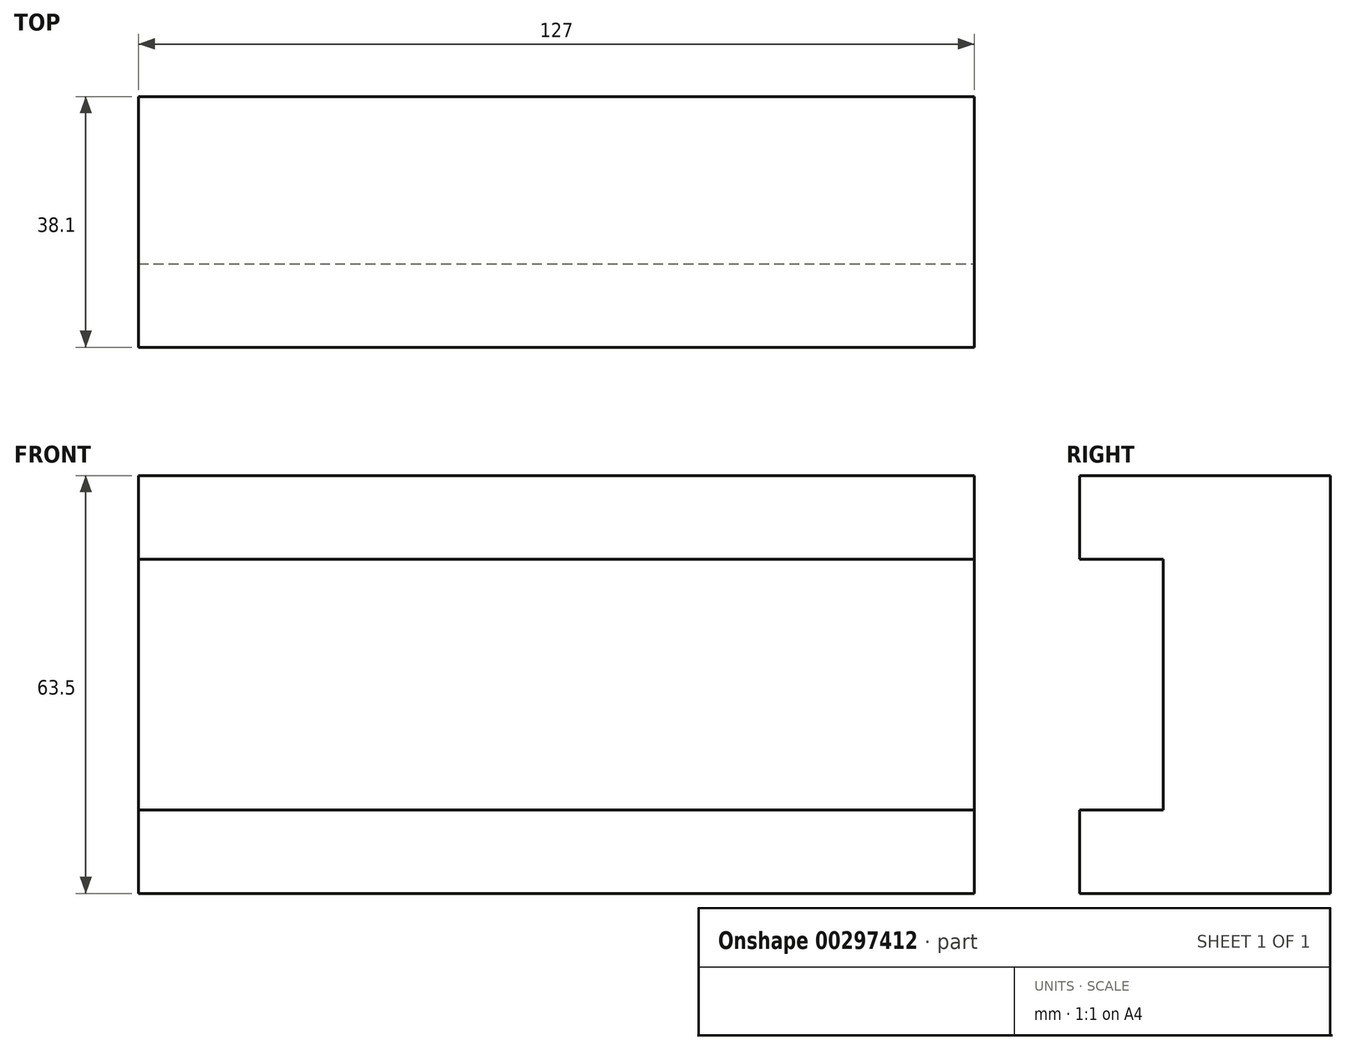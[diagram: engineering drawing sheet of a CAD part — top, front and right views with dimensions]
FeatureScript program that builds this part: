
annotation { "Feature Type Name" : "Feature", "Feature Type Description" : "" }
export const myFeature = defineFeature(function(context is Context, id is Id, definition is map)
    precondition{}
    {
        {
            var Q0;
            Q0=qCreatedBy(makeId("Front.planeOp"),FACE);
            var sketch = newSketch(context, id + "F0", { "sketchPlane" : qUnion([Q0])});
            skLineSegment(sketch, "E0.bottom", {"start": v(-63.5, -31.75) * mm, "end": v(63.5, -31.75) * mm});
            skLineSegment(sketch, "E0.top", {"start": v(-63.5, 31.75) * mm, "end": v(63.5, 31.75) * mm});
            skLineSegment(sketch, "E0.left", {"start": v(-63.5, -31.75) * mm, "end": v(-63.5, 31.75) * mm});
            skLineSegment(sketch, "E0.right", {"start": v(63.5, -31.75) * mm, "end": v(63.5, 31.75) * mm});
            skPoint(sketch, "E0.middle", {"position": v(0, 0) * mm});
            skLineSegment(sketch, "E1.top", {"start": v(-63.5, 19.05) * mm, "end": v(63.5, 19.05) * mm});
            skLineSegment(sketch, "E1.left", {"start": v(-63.5, 31.75) * mm, "end": v(-63.5, 19.05) * mm});
            skLineSegment(sketch, "E1.right", {"start": v(63.5, 31.75) * mm, "end": v(63.5, 19.05) * mm});
            skLineSegment(sketch, "E2.bottom", {"start": v(-63.5, -19.05) * mm, "end": v(63.5, -19.05) * mm});
            skLineSegment(sketch, "E2.left", {"start": v(-63.5, -19.05) * mm, "end": v(-63.5, -31.75) * mm});
            skLineSegment(sketch, "E2.right", {"start": v(63.5, -19.05) * mm, "end": v(63.5, -31.75) * mm});
            skSolve(sketch);
        }
        {
            var Q0;
            Q0 = qSketchRegion(id + "F0", true);
            extrude(context, id + "F1", {"entities" : qUnion([Q0]), "depth" : 25.4 * mm});
        }
        {
            var Q0;
            Q0=makeQuery(id+"F1.opExtrude","CAP_FACE",FACE,{"disambiguationData":[OSD([sQuery(id+"F0.wireOp",EDGE,"E0.left"),sQuery(id+"F0.wireOp",EDGE,"E0.right"),sQuery(id+"F0.wireOp",EDGE,"E0.top"),sQuery(id+"F0.wireOp",EDGE,"E1.left"),sQuery(id+"F0.wireOp",EDGE,"E1.right"),sQuery(id+"F0.wireOp",EDGE,"E0.bottom"),sQuery(id+"F0.wireOp",EDGE,"E2.left"),sQuery(id+"F0.wireOp",EDGE,"E2.right")])],"isStart":false});
            var sketch = newSketch(context, id + "F2", { "sketchPlane" : qUnion([Q0])});
            skLineSegment(sketch, "E3.bottom", {"start": v(-63.5, 31.75) * mm, "end": v(63.5, 31.75) * mm});
            skLineSegment(sketch, "E3.top", {"start": v(-63.5, 19.05) * mm, "end": v(63.5, 19.05) * mm});
            skLineSegment(sketch, "E3.left", {"start": v(-63.5, 31.75) * mm, "end": v(-63.5, 19.05) * mm});
            skLineSegment(sketch, "E3.right", {"start": v(63.5, 31.75) * mm, "end": v(63.5, 19.05) * mm});
            skLineSegment(sketch, "E4.bottom", {"start": v(-63.5, -31.75) * mm, "end": v(63.5, -31.75) * mm});
            skLineSegment(sketch, "E4.top", {"start": v(-63.5, -19.05) * mm, "end": v(63.5, -19.05) * mm});
            skLineSegment(sketch, "E4.left", {"start": v(-63.5, -31.75) * mm, "end": v(-63.5, -19.05) * mm});
            skLineSegment(sketch, "E4.right", {"start": v(63.5, -31.75) * mm, "end": v(63.5, -19.05) * mm});
            skSolve(sketch);
        }
        {
            var Q0;
            Q0=makeQuery(id+"F2.imprint","IMPRINT",FACE,{"disambiguationData":[TD([[makeQuery(id+"F2.imprint","IMPRINT",EDGE,{"derivedFrom":sQuery(id+"F2.wireOp",EDGE,"E3.bottom")}),-1.0]])]});
            extrude(context, id + "F3", {"entities" : qUnion([Q0]), "operationType" : NewBodyOperationType.ADD, "depth" : 12.7 * mm});
        }
        {
            var Q0;
            Q0=makeQuery(id+"F2.imprint","IMPRINT",FACE,{"disambiguationData":[TD([[makeQuery(id+"F2.imprint","IMPRINT",EDGE,{"derivedFrom":sQuery(id+"F2.wireOp",EDGE,"E4.bottom")}),1.0]])]});
            extrude(context, id + "F4", {"entities" : qUnion([Q0]), "operationType" : NewBodyOperationType.ADD, "depth" : 12.7 * mm});
        }
    });
